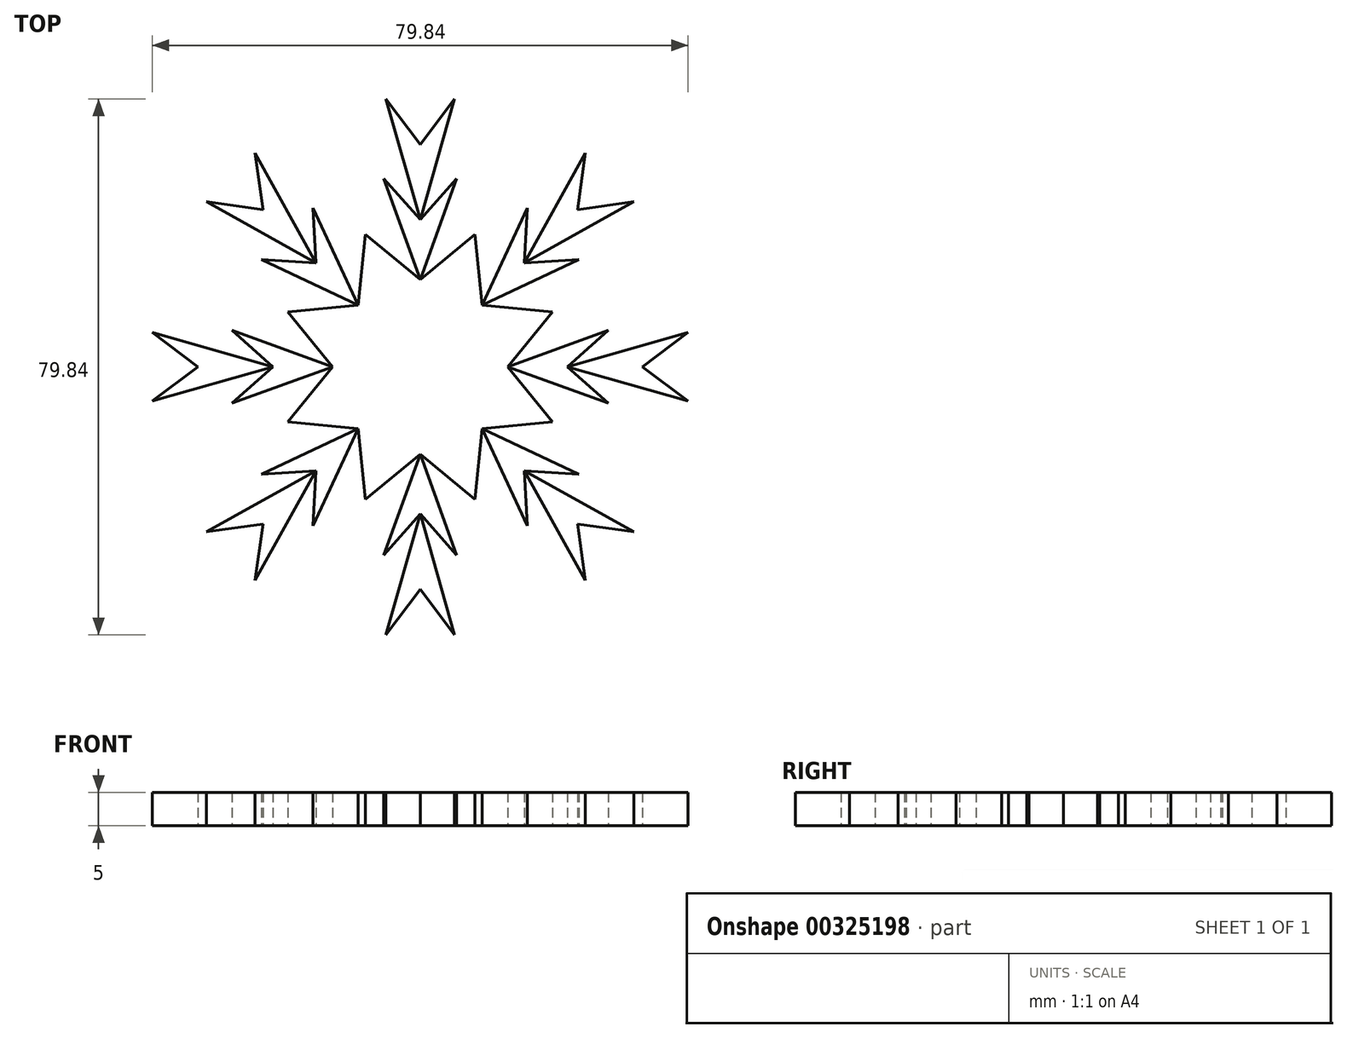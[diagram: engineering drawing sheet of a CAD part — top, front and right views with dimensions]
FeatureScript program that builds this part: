
annotation { "Feature Type Name" : "Feature", "Feature Type Description" : "" }
export const myFeature = defineFeature(function(context is Context, id is Id, definition is map)
    precondition{}
    {
        {
            var Q0;
            Q0=qCreatedBy(makeId("Top.planeOp"),FACE);
            var sketch = newSketch(context, id + "F0", { "sketchPlane" : qUnion([Q0])});
            skLineSegment(sketch, "E0", {"start": v(0, 13.03) * mm, "end": v(10.86, 21.94) * mm});
            skLineSegment(sketch, "E1", {"start": v(0, 21.94) * mm, "end": v(10.23, 33.46) * mm});
            skLineSegment(sketch, "E2", {"start": v(0, 33.13) * mm, "end": v(10.23, 46.7) * mm});
            skLineSegment(sketch, "E3", {"start": v(0, 21.94) * mm, "end": v(5.12, 39.92) * mm});
            skLineSegment(sketch, "E4", {"start": v(0, 13.03) * mm, "end": v(5.43, 28.05) * mm});
            skPoint(sketch, "E4.endSnap0", {"position": v(5.43, 17.49) * mm});
            skLineSegment(sketch, "E5.MirrorCS", {"start": v(0, 33.13) * mm, "end": v(-10.23, 46.7) * mm});
            skLineSegment(sketch, "E6.MirrorCS", {"start": v(0, 21.94) * mm, "end": v(-5.12, 39.92) * mm});
            skLineSegment(sketch, "E7.MirrorCS", {"start": v(0, 21.94) * mm, "end": v(-10.23, 33.46) * mm});
            skLineSegment(sketch, "E8.MirrorCS", {"start": v(0, 13.03) * mm, "end": v(-5.43, 28.05) * mm});
            skLineSegment(sketch, "E9.MirrorCS", {"start": v(0, 13.03) * mm, "end": v(-10.86, 21.94) * mm});
            skLineSegment(sketch, "E10.1.0", {"start": v(-23.43, 23.43) * mm, "end": v(-40.26, 25.79) * mm});
            skLineSegment(sketch, "E10.1.1", {"start": v(-23.43, 23.43) * mm, "end": v(-25.79, 40.26) * mm});
            skLineSegment(sketch, "E10.1.2", {"start": v(-15.51, 15.51) * mm, "end": v(-31.84, 24.6) * mm});
            skLineSegment(sketch, "E10.1.3", {"start": v(-15.51, 15.51) * mm, "end": v(-24.6, 31.84) * mm});
            skLineSegment(sketch, "E10.1.4", {"start": v(-15.51, 15.51) * mm, "end": v(-30.9, 16.42) * mm});
            skLineSegment(sketch, "E10.1.5", {"start": v(-15.51, 15.51) * mm, "end": v(-16.42, 30.9) * mm});
            skLineSegment(sketch, "E10.1.6", {"start": v(-9.22, 9.22) * mm, "end": v(-16, 23.68) * mm});
            skLineSegment(sketch, "E10.1.7", {"start": v(-9.22, 9.22) * mm, "end": v(-23.68, 16) * mm});
            skLineSegment(sketch, "E10.1.8", {"start": v(-9.22, 9.22) * mm, "end": v(-23.2, 7.83) * mm});
            skLineSegment(sketch, "E10.1.9", {"start": v(-9.22, 9.22) * mm, "end": v(-7.83, 23.2) * mm});
            skLineSegment(sketch, "E10.2.0", {"start": v(-33.13, 0) * mm, "end": v(-46.7, -10.23) * mm});
            skLineSegment(sketch, "E10.2.1", {"start": v(-33.13, 0) * mm, "end": v(-46.7, 10.23) * mm});
            skLineSegment(sketch, "E10.2.2", {"start": v(-21.94, 0) * mm, "end": v(-39.92, -5.12) * mm});
            skLineSegment(sketch, "E10.2.3", {"start": v(-21.94, 0) * mm, "end": v(-39.92, 5.12) * mm});
            skLineSegment(sketch, "E10.2.4", {"start": v(-21.94, 0) * mm, "end": v(-33.46, -10.23) * mm});
            skLineSegment(sketch, "E10.2.5", {"start": v(-21.94, 0) * mm, "end": v(-33.46, 10.23) * mm});
            skLineSegment(sketch, "E10.2.6", {"start": v(-13.03, 0) * mm, "end": v(-28.05, 5.43) * mm});
            skLineSegment(sketch, "E10.2.7", {"start": v(-13.03, 0) * mm, "end": v(-28.05, -5.43) * mm});
            skLineSegment(sketch, "E10.2.8", {"start": v(-13.03, 0) * mm, "end": v(-21.94, -10.86) * mm});
            skLineSegment(sketch, "E10.2.9", {"start": v(-13.03, 0) * mm, "end": v(-21.94, 10.86) * mm});
            skLineSegment(sketch, "E10.3.0", {"start": v(-23.43, -23.43) * mm, "end": v(-25.79, -40.26) * mm});
            skLineSegment(sketch, "E10.3.1", {"start": v(-23.43, -23.43) * mm, "end": v(-40.26, -25.79) * mm});
            skLineSegment(sketch, "E10.3.2", {"start": v(-15.51, -15.51) * mm, "end": v(-24.6, -31.84) * mm});
            skLineSegment(sketch, "E10.3.3", {"start": v(-15.51, -15.51) * mm, "end": v(-31.84, -24.6) * mm});
            skLineSegment(sketch, "E10.3.4", {"start": v(-15.51, -15.51) * mm, "end": v(-16.42, -30.9) * mm});
            skLineSegment(sketch, "E10.3.5", {"start": v(-15.51, -15.51) * mm, "end": v(-30.9, -16.42) * mm});
            skLineSegment(sketch, "E10.3.6", {"start": v(-9.22, -9.22) * mm, "end": v(-23.68, -16) * mm});
            skLineSegment(sketch, "E10.3.7", {"start": v(-9.22, -9.22) * mm, "end": v(-16, -23.68) * mm});
            skLineSegment(sketch, "E10.3.8", {"start": v(-9.22, -9.22) * mm, "end": v(-7.83, -23.2) * mm});
            skLineSegment(sketch, "E10.3.9", {"start": v(-9.22, -9.22) * mm, "end": v(-23.2, -7.83) * mm});
            skLineSegment(sketch, "E10.4.0", {"start": v(0, -33.13) * mm, "end": v(10.23, -46.7) * mm});
            skLineSegment(sketch, "E10.4.1", {"start": v(0, -33.13) * mm, "end": v(-10.23, -46.7) * mm});
            skLineSegment(sketch, "E10.4.2", {"start": v(0, -21.94) * mm, "end": v(5.12, -39.92) * mm});
            skLineSegment(sketch, "E10.4.3", {"start": v(0, -21.94) * mm, "end": v(-5.12, -39.92) * mm});
            skLineSegment(sketch, "E10.4.4", {"start": v(0, -21.94) * mm, "end": v(10.23, -33.46) * mm});
            skLineSegment(sketch, "E10.4.5", {"start": v(0, -21.94) * mm, "end": v(-10.23, -33.46) * mm});
            skLineSegment(sketch, "E10.4.6", {"start": v(0, -13.03) * mm, "end": v(-5.43, -28.05) * mm});
            skLineSegment(sketch, "E10.4.7", {"start": v(0, -13.03) * mm, "end": v(5.43, -28.05) * mm});
            skLineSegment(sketch, "E10.4.8", {"start": v(0, -13.03) * mm, "end": v(10.86, -21.94) * mm});
            skLineSegment(sketch, "E10.4.9", {"start": v(0, -13.03) * mm, "end": v(-10.86, -21.94) * mm});
            skLineSegment(sketch, "E10.5.0", {"start": v(23.43, -23.43) * mm, "end": v(40.26, -25.79) * mm});
            skLineSegment(sketch, "E10.5.1", {"start": v(23.43, -23.43) * mm, "end": v(25.79, -40.26) * mm});
            skLineSegment(sketch, "E10.5.2", {"start": v(15.51, -15.51) * mm, "end": v(31.84, -24.6) * mm});
            skLineSegment(sketch, "E10.5.3", {"start": v(15.51, -15.51) * mm, "end": v(24.6, -31.84) * mm});
            skLineSegment(sketch, "E10.5.4", {"start": v(15.51, -15.51) * mm, "end": v(30.9, -16.42) * mm});
            skLineSegment(sketch, "E10.5.5", {"start": v(15.51, -15.51) * mm, "end": v(16.42, -30.9) * mm});
            skLineSegment(sketch, "E10.5.6", {"start": v(9.22, -9.22) * mm, "end": v(16, -23.68) * mm});
            skLineSegment(sketch, "E10.5.7", {"start": v(9.22, -9.22) * mm, "end": v(23.68, -16) * mm});
            skLineSegment(sketch, "E10.5.8", {"start": v(9.22, -9.22) * mm, "end": v(23.2, -7.83) * mm});
            skLineSegment(sketch, "E10.5.9", {"start": v(9.22, -9.22) * mm, "end": v(7.83, -23.2) * mm});
            skLineSegment(sketch, "E10.6.0", {"start": v(33.13, 0) * mm, "end": v(46.7, 10.23) * mm});
            skLineSegment(sketch, "E10.6.1", {"start": v(33.13, 0) * mm, "end": v(46.7, -10.23) * mm});
            skLineSegment(sketch, "E10.6.2", {"start": v(21.94, 0) * mm, "end": v(39.92, 5.12) * mm});
            skLineSegment(sketch, "E10.6.3", {"start": v(21.94, 0) * mm, "end": v(39.92, -5.12) * mm});
            skLineSegment(sketch, "E10.6.4", {"start": v(21.94, 0) * mm, "end": v(33.46, 10.23) * mm});
            skLineSegment(sketch, "E10.6.5", {"start": v(21.94, 0) * mm, "end": v(33.46, -10.23) * mm});
            skLineSegment(sketch, "E10.6.6", {"start": v(13.03, 0) * mm, "end": v(28.05, -5.43) * mm});
            skLineSegment(sketch, "E10.6.7", {"start": v(13.03, 0) * mm, "end": v(28.05, 5.43) * mm});
            skLineSegment(sketch, "E10.6.8", {"start": v(13.03, 0) * mm, "end": v(21.94, 10.86) * mm});
            skLineSegment(sketch, "E10.6.9", {"start": v(13.03, 0) * mm, "end": v(21.94, -10.86) * mm});
            skLineSegment(sketch, "E10.7.0", {"start": v(23.43, 23.43) * mm, "end": v(25.79, 40.26) * mm});
            skLineSegment(sketch, "E10.7.1", {"start": v(23.43, 23.43) * mm, "end": v(40.26, 25.79) * mm});
            skLineSegment(sketch, "E10.7.2", {"start": v(15.51, 15.51) * mm, "end": v(24.6, 31.84) * mm});
            skLineSegment(sketch, "E10.7.3", {"start": v(15.51, 15.51) * mm, "end": v(31.84, 24.6) * mm});
            skLineSegment(sketch, "E10.7.4", {"start": v(15.51, 15.51) * mm, "end": v(16.42, 30.9) * mm});
            skLineSegment(sketch, "E10.7.5", {"start": v(15.51, 15.51) * mm, "end": v(30.9, 16.42) * mm});
            skLineSegment(sketch, "E10.7.6", {"start": v(9.22, 9.22) * mm, "end": v(23.68, 16) * mm});
            skLineSegment(sketch, "E10.7.7", {"start": v(9.22, 9.22) * mm, "end": v(16, 23.68) * mm});
            skLineSegment(sketch, "E10.7.8", {"start": v(9.22, 9.22) * mm, "end": v(7.83, 23.2) * mm});
            skLineSegment(sketch, "E10.7.9", {"start": v(9.22, 9.22) * mm, "end": v(23.2, 7.83) * mm});
            skPoint(sketch, "E10.center", {"position": v(0, 0) * mm});
            skSolve(sketch);
        }
        {
            var Q0;
            Q0 = qSketchRegion(id + "F0", true);
            extrude(context, id + "F1", {"entities" : qUnion([Q0]), "endBound" : BoundingType.SYMMETRIC, "depth" : 5 * mm});
        }
    });
